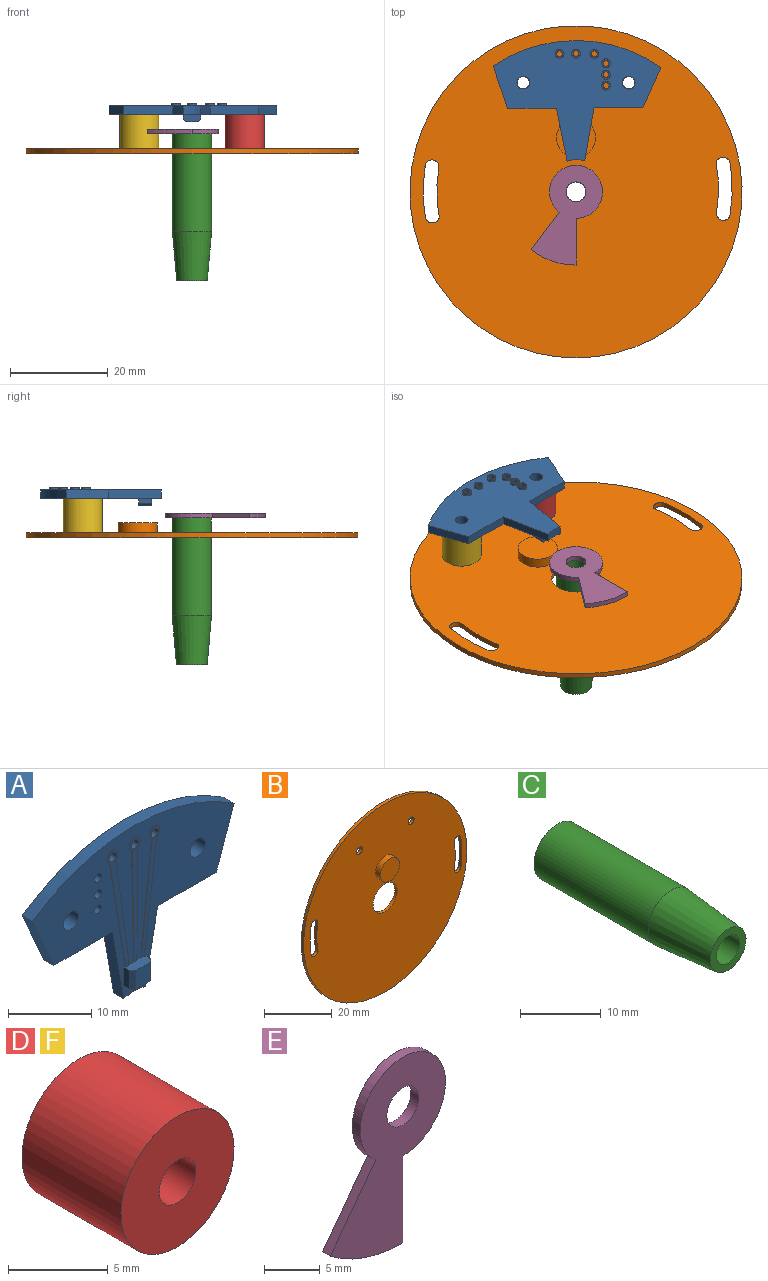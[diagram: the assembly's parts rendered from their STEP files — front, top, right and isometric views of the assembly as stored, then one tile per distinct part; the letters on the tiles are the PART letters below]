
ASSEMBLY  parts=6 mates=5
PART A: 58 faces, bbox 34.4x3.8x24.7 mm
  f0: plane 34.37x24.66mm, normal (0,-1,0), area 381.5mm2, adj f2,f3,f4,f5,f6,f7,f8,f9
  f1: plane 34.37x24.66mm, normal (0,1,0), area 422.1mm2, adj f2,f3,f4,f5,f6,f7,f8,f9
  f2: plane 10.86x1.93mm, normal (-0.98,0,-0.18), area 19.3mm2, adj f0,f1,f3,f9
  f3: cylinder r=6mm len=3.61mm, axis (0,1,0), area 6.4mm2, adj f0,f1,f2,f4
  f4: plane 10.81x2.15mm, normal (0.98,0,-0.19), area 19.3mm2, adj f0,f1,f3,f5
  f5: plane 10x1.75mm, normal (0,0,-1), area 17.5mm2, adj f0,f1,f4,f6
  f6: plane 8.65x3mm, normal (0.94,0,-0.33), area 16mm2, adj f0,f1,f5,f7
  f7: cylinder r=30.37mm len=34.37mm, axis (0,1,0), area 63.9mm2, adj f0,f1,f6,f8
  f8: plane 8.31x3.68mm, normal (-0.91,0,-0.4), area 15.9mm2, adj f0,f1,f7,f9
  f9: plane 10x1.75mm, normal (0,0,-1), area 17.5mm2, adj f0,f1,f2,f8
  f10: plane 2.73x1mm, normal (-1,0,0), area 2.7mm2, adj f0,f11,f13,f21
  f11: plane 3.55x1.5mm, normal (0,0,-1), area 5.1mm2, adj f0,f10,f12,f14,f20,f21
  f12: plane 2.73x1mm, normal (1,0,0), area 2.7mm2, adj f0,f11,f13,f20
  f13: plane 3.55x1.5mm, normal (0,0,1), area 4.9mm2, adj f0,f10,f12,f14,f20,f21,f23,f24
  f14: plane 2.73x2.55mm, normal (0,-1,0), area 6.9mm2, adj f11,f13,f20,f21
  f15: cylinder r=1.3mm len=2.6mm, axis (0,1,0), area 14.3mm2, adj f0,f1
  f16: cylinder r=1.3mm len=2.6mm, axis (0,1,0), area 14.3mm2, adj f0,f1
  f17: cylinder r=0.6mm len=2.35mm, axis (0,1,0), area 8.9mm2, adj f28,f47
  f18: cylinder r=0.6mm len=2.35mm, axis (0,1,0), area 8.9mm2, adj f42,f49
  f19: cylinder r=0.6mm len=2.35mm, axis (0,1,0), area 8.9mm2, adj f36,f51
  f20: plane 2.73x0.5mm, normal (0.71,-0.71,0), area 1.9mm2, adj f11,f12,f13,f14
  f21: plane 2.73x0.5mm, normal (-0.71,-0.71,0), area 1.9mm2, adj f10,f11,f13,f14
  f22: plane 15.45x1.75mm, normal (-0.99,0,0.11), area 1.6mm2, adj f0,f23,f27,f28
  f23: plane 1.12x0.1mm, normal (-1,0,0), area 0.1mm2, adj f0,f13,f22,f28
  f24: plane 1.12x0.1mm, normal (1,0,0), area 0.1mm2, adj f0,f13,f25,f28
  f25: plane 0.13x0.1mm, normal (0,0,-1), area 0mm2, adj f0,f24,f26,f28
  f26: plane 15.41x1.94mm, normal (0.99,0,-0.12), area 1.6mm2, adj f0,f25,f27,f28
  f27: cylinder r=0.88mm len=1.75mm, axis (0,1,0), area 0.5mm2, adj f0,f22,f26,f28
  f28: plane 18.21x3.05mm, normal (0,-1,0), area 12.2mm2, adj f13,f17,f22,f23,f24,f25,f26,f27
  f29: plane 1.12x0.1mm, normal (1,0,0), area 0.1mm2, adj f0,f13,f30,f36
  f30: plane 0.1x0mm, normal (0,0,-1), area 0mm2, adj f0,f29,f31,f36
  f31: plane 15.5x2.16mm, normal (0.99,0,0.14), area 1.6mm2, adj f0,f30,f32,f36
  f32: cylinder r=0.88mm len=1.75mm, axis (0,1,0), area 0.4mm2, adj f0,f31,f33,f36
  f33: plane 15.49x2.47mm, normal (-0.99,0,-0.16), area 1.6mm2, adj f0,f32,f34,f36
  f34: plane 0.14x0.1mm, normal (0,0,-1), area 0mm2, adj f0,f33,f35,f36
  f35: plane 1.12x0.1mm, normal (-1,0,0), area 0.1mm2, adj f0,f13,f34,f36
  f36: plane 18.21x3.54mm, normal (0,-1,0), area 14.8mm2, adj f13,f19,f29,f30,f31,f32,f33,f34
  f37: plane 1.12x0.1mm, normal (1,0,0), area 0.1mm2, adj f0,f13,f38,f42
  f38: plane 15.47x0.13mm, normal (1,0,-0.01), area 1.5mm2, adj f0,f37,f39,f42
  f39: cylinder r=0.88mm len=1.75mm, axis (0,1,0), area 0.5mm2, adj f0,f38,f40,f42
  f40: plane 15.46x0.3mm, normal (-1,0,-0.02), area 1.5mm2, adj f0,f39,f41,f42
  f41: plane 1.12x0.1mm, normal (-1,0,0), area 0.1mm2, adj f0,f13,f40,f42
  f42: plane 18.21x1.75mm, normal (0,-1,0), area 12.7mm2, adj f13,f18,f37,f38,f39,f40,f41
  f43: cylinder r=0.6mm len=2.25mm, axis (0,1,0), area 8.5mm2, adj f0,f57
  f44: cylinder r=0.6mm len=2.25mm, axis (0,1,0), area 8.5mm2, adj f0,f55
  f45: cylinder r=0.6mm len=2.25mm, axis (0,1,0), area 8.5mm2, adj f0,f53
  f46: cylinder r=0.91mm len=1.82mm, axis (0,-1,0), area 2.9mm2, adj f1,f47
  f47: plane 1.82x1.82mm, normal (0,1,0), area 1.5mm2, adj f17,f46
  f48: cylinder r=0.91mm len=1.82mm, axis (0,-1,0), area 2.9mm2, adj f1,f49
  f49: plane 1.82x1.82mm, normal (0,1,0), area 1.5mm2, adj f18,f48
  f50: cylinder r=0.91mm len=1.82mm, axis (0,-1,0), area 2.9mm2, adj f1,f51
  f51: plane 1.82x1.82mm, normal (0,1,0), area 1.5mm2, adj f19,f50
  f52: cylinder r=0.91mm len=1.82mm, axis (0,-1,0), area 2.9mm2, adj f1,f53
  f53: plane 1.82x1.82mm, normal (0,1,0), area 1.5mm2, adj f45,f52
  f54: cylinder r=0.91mm len=1.82mm, axis (0,-1,0), area 2.9mm2, adj f1,f55
  f55: plane 1.82x1.82mm, normal (0,1,0), area 1.5mm2, adj f44,f54
  f56: cylinder r=0.91mm len=1.82mm, axis (0,-1,0), area 2.9mm2, adj f1,f57
  f57: plane 1.82x1.82mm, normal (0,1,0), area 1.5mm2, adj f43,f56
PART B: 16 faces, bbox 68x3x68 mm
  f0: cylinder r=1.43mm len=2.86mm, axis (0,1,0), area 4.9mm2, adj f1,f7,f10,f11
  f1: cylinder r=28.49mm len=10.28mm, axis (0,1,0), area 10.3mm2, adj f0,f2,f10,f11
  f2: cylinder r=1.5mm len=2.85mm, axis (0,1,0), area 3.7mm2, adj f1,f7,f10,f11
  f3: cylinder r=1.43mm len=2.86mm, axis (0,1,0), area 4.9mm2, adj f4,f8,f10,f11
  f4: cylinder r=28.49mm len=10.28mm, axis (0,1,0), area 10.3mm2, adj f3,f5,f10,f11
  f5: cylinder r=1.5mm len=2.85mm, axis (0,1,0), area 3.7mm2, adj f4,f8,f10,f11
  f6: cylinder r=5mm len=10mm, axis (0,1,0), area 31.4mm2, adj f10,f11
  f7: cylinder r=31.29mm len=10.26mm, axis (0,1,0), area 10.3mm2, adj f0,f2,f10,f11
  f8: cylinder r=31.29mm len=10.26mm, axis (0,1,0), area 10.3mm2, adj f3,f5,f10,f11
  f9: cylinder r=33.99mm len=67.98mm, axis (0,1,0), area 213.6mm2, adj f10,f11
  f10: plane 67.98x67.98mm, normal (0,-1,0), area 3421.6mm2, adj f0,f1,f2,f3,f4,f5,f6,f7
  f11: plane 67.98x67.98mm, normal (0,1,0), area 3471.9mm2, adj f0,f1,f2,f3,f4,f5,f6,f7
  f12: cylinder r=4mm len=8mm, axis (0,1,0), area 50.3mm2, adj f10,f13
  f13: plane 8x8mm, normal (0,-1,0), area 50.3mm2, adj f12
  f14: cylinder r=1.25mm len=2.5mm, axis (0,-1,0), area 7.9mm2, adj f10,f11
  f15: cylinder r=1.25mm len=2.5mm, axis (0,-1,0), area 7.9mm2, adj f10,f11
PART C: 5 faces, bbox 8.1x30x8.1 mm
  f0: cylinder r=4.03mm len=20mm, axis (0,-1,0), area 506.4mm2, adj f1,f4
  f1: cone r=4.03mm half-angle=5.1deg, axis (0,1,0), area 226.2mm2, adj f0,f2
  f2: plane 6.28x6.28mm, normal (0,-1,0), area 18.1mm2, adj f1,f3
  f3: cylinder r=2.03mm len=30mm, axis (0,-1,0), area 382.6mm2, adj f2,f4
  f4: plane 8.06x8.06mm, normal (0,1,0), area 38.1mm2, adj f0,f3
PART D: 4 faces, bbox 8x7x8 mm
  f0: cylinder r=1.3mm len=7mm, axis (0,1,0), area 57.2mm2, adj f2,f3
  f1: cylinder r=4mm len=8mm, axis (0,1,0), area 175.9mm2, adj f2,f3
  f2: plane 8x8mm, normal (0,-1,0), area 45mm2, adj f0,f1
  f3: plane 8x8mm, normal (0,1,0), area 45mm2, adj f0,f1
PART E: 7 faces, bbox 14.6x1x20.4 mm
  f0: plane 9.59x1mm, normal (1,0,0), area 9.6mm2, adj f1,f3,f5,f6
  f1: cylinder r=5.41mm len=10.83mm, axis (0,1,0), area 30.3mm2, adj f0,f2,f5,f6
  f2: plane 7.69x5.73mm, normal (-0.8,0,0.6), area 9.6mm2, adj f1,f3,f5,f6
  f3: cylinder r=15mm len=9.2mm, axis (0,1,0), area 9.9mm2, adj f0,f2,f5,f6
  f4: cylinder r=2.03mm len=4.06mm, axis (0,1,0), area 12.8mm2, adj f5,f6
  f5: plane 20.42x14.61mm, normal (0,-1,0), area 144.6mm2, adj f0,f1,f2,f3,f4
  f6: plane 20.42x14.61mm, normal (0,1,0), area 144.6mm2, adj f0,f1,f2,f3,f4
PART F: same geometry as D
PLACE A rot(axis=(0,0.71,0.71),180deg) t=(0,0.57,8.75)mm
PLACE B rot(axis=(-1,0,0),90deg) t=(0,0,-1)mm
PLACE C rot(axis=(1,0,0),90deg) t=(0,0,-17)mm
PLACE D rot(axis=(-1,0,0),90deg) t=(10.78,22.33,0)mm
PLACE E rot(axis=(-1,0,0),90deg) t=(0,0,3)mm
PLACE F rot(axis=(-1,0,0),90deg) t=(-10.78,22.33,0)mm
MATE fastened B.f14 <-> D.f0  axis (0,0,1) through (10.78,22.33,0)mm
MATE fastened A.f15 <-> F.f1  axis (0,0,-1) through (-10.78,22.33,7)mm
MATE fastened E.f4 <-> C.f0  axis (0,0,-1) through (0,0,3)mm
MATE revolute B.f6 <-> C.f0  axis (0,0,1) through (0,0,0)mm
MATE fastened B.f15 <-> F.f1  axis (0,0,1) through (-10.78,22.33,0)mm
